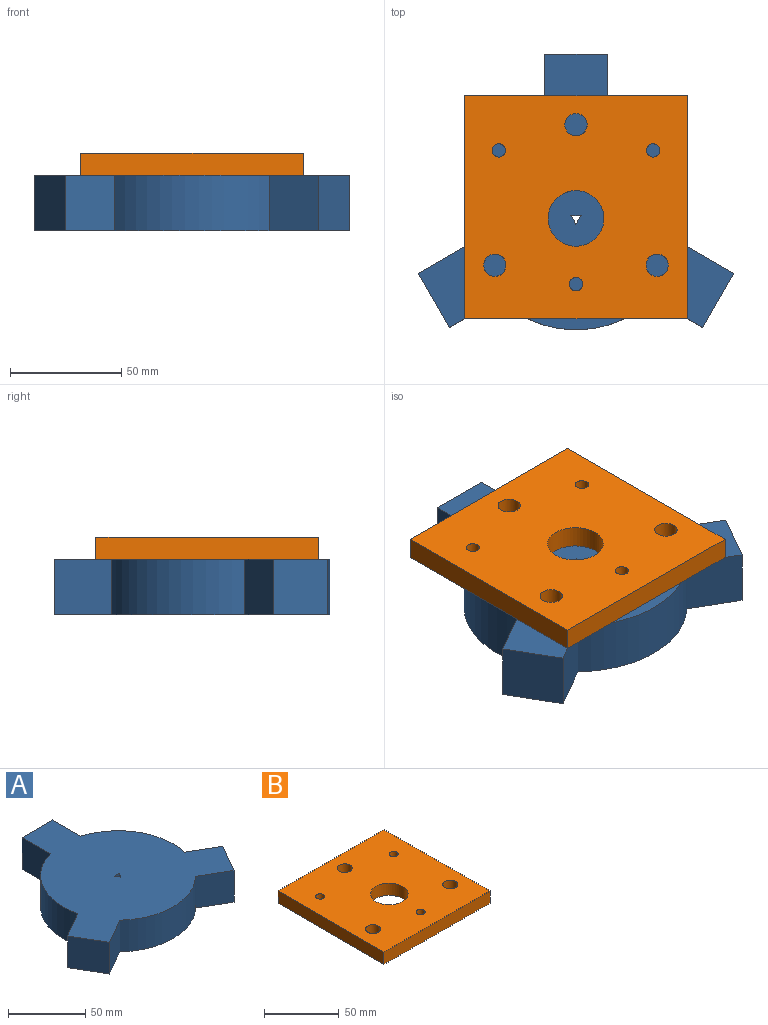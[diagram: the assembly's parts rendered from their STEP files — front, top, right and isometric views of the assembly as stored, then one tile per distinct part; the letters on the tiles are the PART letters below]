
ASSEMBLY  parts=2 mates=1
PART A: 17 faces, bbox 141.6x123.7x25 mm
  f0: plane 25x4.57mm, normal (0,-1,0), area 114.2mm2, adj f1,f14,f15,f16
  f1: plane 25x3.95mm, normal (-0.87,0.5,0), area 114.2mm2, adj f0,f14,f15,f16
  f2: plane 28x25mm, normal (0,1,0), area 700mm2, adj f3,f13,f15,f16
  f3: plane 25.68x25mm, normal (-1,0,0), area 642mm2, adj f2,f4,f15,f16
  f4: cylinder r=50mm len=59.88mm, axis (0,0,-1), area 1908.5mm2, adj f3,f5,f15,f16
  f5: plane 25x22.24mm, normal (-0.5,0.87,0), area 642mm2, adj f4,f6,f15,f16
  f6: plane 25x24.25mm, normal (-0.87,-0.5,0), area 700mm2, adj f5,f7,f15,f16
  f7: plane 25x22.24mm, normal (0.5,-0.87,0), area 642mm2, adj f6,f8,f15,f16
  f8: cylinder r=50mm len=69.14mm, axis (0,0,-1), area 1908.5mm2, adj f7,f9,f15,f16
  f9: plane 25x22.24mm, normal (-0.5,-0.87,0), area 642mm2, adj f8,f10,f15,f16
  f10: plane 25x24.25mm, normal (0.87,-0.5,0), area 700mm2, adj f9,f11,f15,f16
  f11: plane 25x22.24mm, normal (0.5,0.87,0), area 642mm2, adj f10,f12,f15,f16
  f12: cylinder r=50mm len=59.88mm, axis (0,0,-1), area 1908.5mm2, adj f11,f13,f15,f16
  f13: plane 25.68x25mm, normal (1,0,0), area 642mm2, adj f2,f12,f15,f16
  f14: plane 25x3.95mm, normal (0.87,0.5,0), area 114.2mm2, adj f0,f1,f15,f16
  f15: plane 141.62x123.68mm, normal (0,0,1), area 9889.8mm2, adj f0,f1,f2,f3,f4,f5,f6,f7
  f16: plane 141.62x123.68mm, normal (0,0,-1), area 9889.8mm2, adj f0,f1,f2,f3,f4,f5,f6,f7
PART B: 13 faces, bbox 100x100x10 mm
  f0: plane 100x10mm, normal (1,0,0), area 1000mm2, adj f1,f3,f5,f6
  f1: plane 100x10mm, normal (0,1,0), area 1000mm2, adj f0,f2,f5,f6
  f2: plane 100x10mm, normal (-1,0,0), area 1000mm2, adj f1,f3,f5,f6
  f3: plane 100x10mm, normal (0,-1,0), area 1000mm2, adj f0,f2,f5,f6
  f4: cylinder r=12.5mm len=25mm, axis (0,0,-1), area 785.4mm2, adj f5,f6
  f5: plane 100x100mm, normal (0,0,1), area 9188.7mm2, adj f0,f1,f2,f3,f4,f7,f8,f9
  f6: plane 100x100mm, normal (0,0,-1), area 9188.7mm2, adj f0,f1,f2,f3,f4,f7,f8,f9
  f7: cylinder r=5mm len=10mm, axis (0,0,-1), area 314.2mm2, adj f5,f6
  f8: cylinder r=5mm len=10mm, axis (0,0,-1), area 314.2mm2, adj f5,f6
  f9: cylinder r=5mm len=10mm, axis (0,0,-1), area 314.2mm2, adj f5,f6
  f10: cylinder r=3mm len=10mm, axis (0,0,-1), area 188.5mm2, adj f5,f6
  f11: cylinder r=3mm len=10mm, axis (0,0,-1), area 188.5mm2, adj f5,f6
  f12: cylinder r=3mm len=10mm, axis (0,0,-1), area 188.5mm2, adj f5,f6
PLACE A t=(-40.67,46.54,-20.01)mm
PLACE B t=(110.69,46.54,4.99)mm
MATE fastened B.f4 <-> A.f8  axis (0,0,-1) through (110.69,46.54,4.99)mm
